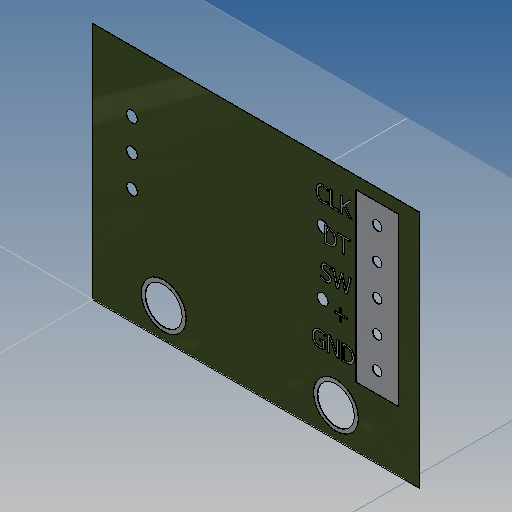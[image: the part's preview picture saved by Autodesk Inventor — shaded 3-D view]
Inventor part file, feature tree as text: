
AUTODESK INVENTOR PART (.ipt)
format: ipt  version: 2019 (Build 230136000, 136)  size: 409,088 bytes
history: native  units: in
note: dims shown in document units (in); Inventor stores cm internally (conversion verified against a paired STEP export)
features: reference x8, extrude x3, sketch x2
ambient origin geometry x8: Origin, YZ Plane, XZ Plane, XY Plane, X Axis, Y Axis, Z Axis, Center Point
bodies: Solid1 (feature_tree)
feature tree (13):
  extrude  "Extrusion1"  Depth=0.14in
  extrude  "Extrusion2"  Depth=0.001in
  extrude  "Extrusion3"  Depth=0.001in
  sketch  "Sketch3"  dims[d0=0.14in d1=0.14in]
  reference  "Reference1"
  sketch  "Sketch4"  dims[d2=0.13in d3=0.53in d4=0.4in d5=0.53in d7=0.1in d8=0.1in d9=0.1in d10=0.1in d11=0.065in d12=0.001in d13=0.0in d14=0.135in d15=0.53in d16=0.0675in d17=0.065in d18=0.4in d19=0.143in d20=0.001in d21=0.0in d22=0.035in d23=0.035in d24=0.001in d25=0.0in d26=0.0in d27=0.1in d28=0.1in]
  reference  "Reference2"
  reference  "Reference3"
  reference  "Reference4"
  reference  "Reference5"
  reference  "Reference6"
  reference  "Reference7"
  reference  "Reference8"
